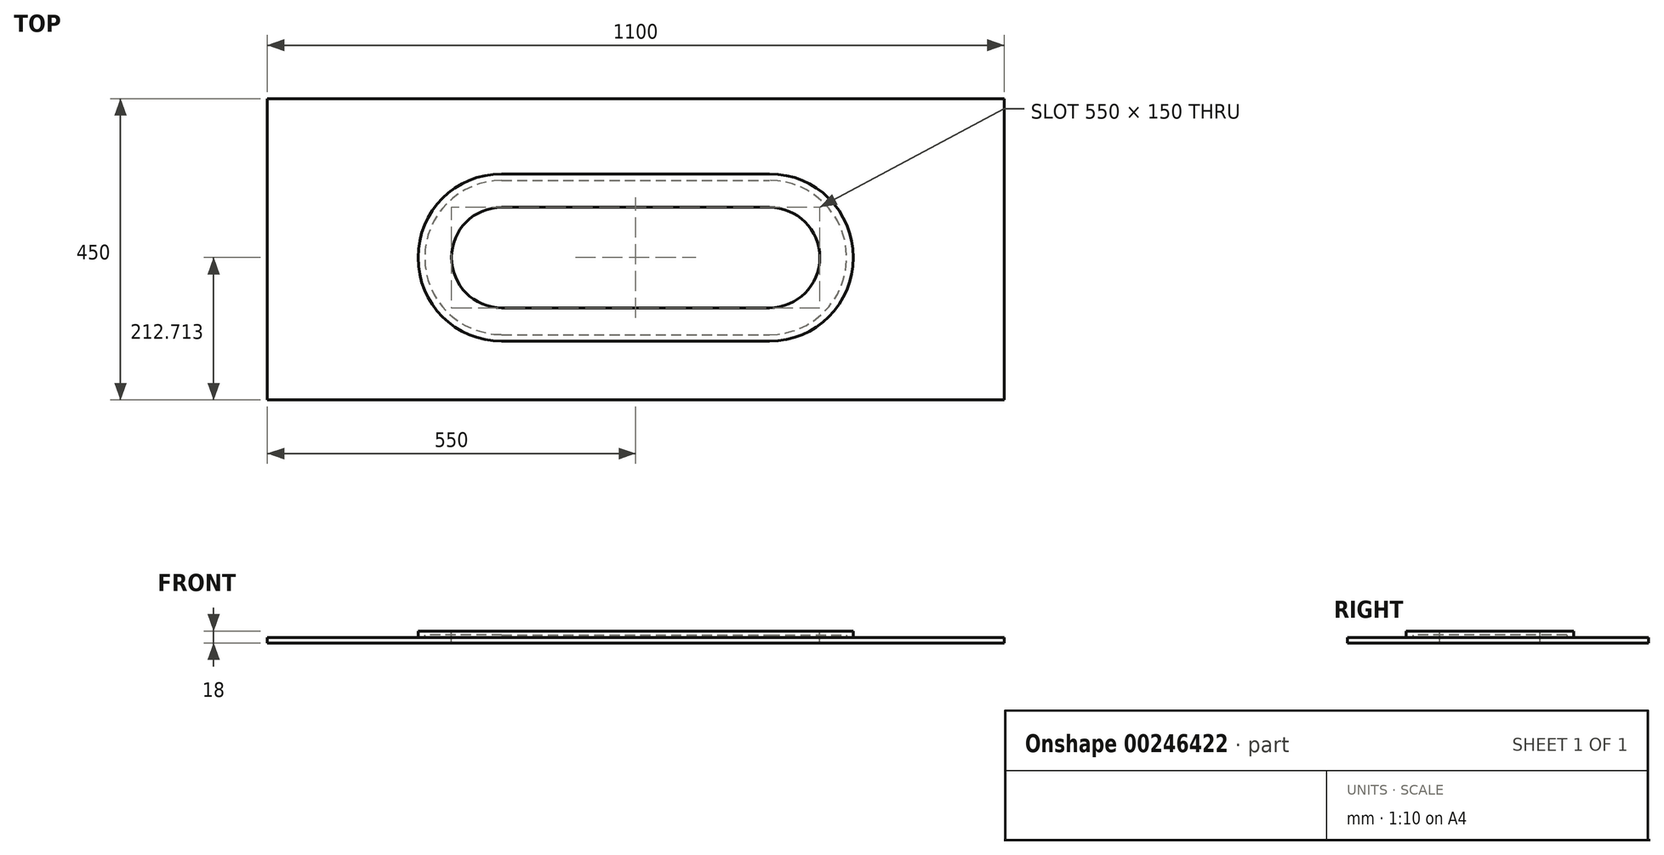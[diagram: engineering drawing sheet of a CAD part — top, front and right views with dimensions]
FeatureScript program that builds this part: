
annotation { "Feature Type Name" : "Feature", "Feature Type Description" : "" }
export const myFeature = defineFeature(function(context is Context, id is Id, definition is map)
    precondition{}
    {
        {
            var Q0;
            Q0=qCreatedBy(makeId("Top.planeOp"),FACE);
            var sketch = newSketch(context, id + "F0", { "sketchPlane" : qUnion([Q0])});
            skLineSegment(sketch, "E0.bottom", {"start": v(0, 0) * mm, "end": v(-1100, 0) * mm});
            skLineSegment(sketch, "E0.top", {"start": v(0, 450) * mm, "end": v(-1100, 450) * mm});
            skLineSegment(sketch, "E0.left", {"start": v(0, 0) * mm, "end": v(0, 450) * mm});
            skLineSegment(sketch, "E0.right", {"start": v(-1100, 0) * mm, "end": v(-1100, 450) * mm});
            skSolve(sketch);
        }
        {
            var Q0;
            Q0 = qSketchRegion(id + "F0", true);
            extrude(context, id + "F1", {"entities" : qUnion([Q0]), "depth" : 18 * mm});
        }
        {
            var Q0;
            Q0=makeQuery(id+"F1.opExtrude","CAP_FACE",FACE,{"disambiguationData":[OSD([sQuery(id+"F0.wireOp",EDGE,"E0.bottom"),sQuery(id+"F0.wireOp",EDGE,"E0.top"),sQuery(id+"F0.wireOp",EDGE,"E0.left"),sQuery(id+"F0.wireOp",EDGE,"E0.right")])],"isStart":false});
            var sketch = newSketch(context, id + "F2", { "sketchPlane" : qUnion([Q0])});
            skLineSegment(sketch, "E1.bottom", {"start": v(-750, 287.71) * mm, "end": v(-350, 287.71) * mm});
            skLineSegment(sketch, "E1.top", {"start": v(-750, 137.71) * mm, "end": v(-350, 137.71) * mm});
            skArc(sketch, "E2", {"start": v(-350, 287.71) * mm, "mid": v(-275, 212.71) * mm, "end": v(-350, 137.71) * mm});
            skArc(sketch, "E3", {"start": v(-750, 287.71) * mm, "mid": v(-825, 212.71) * mm, "end": v(-750, 137.71) * mm});
            skSolve(sketch);
        }
        {
            var Q0;
            Q0 = qSketchRegion(id + "F2", true);
            extrude(context, id + "F3", {"entities" : qUnion([Q0]), "operationType" : NewBodyOperationType.REMOVE, "endBound" : BoundingType.THROUGH_ALL, "oppositeDirection" : true, "depth" : 25 * mm});
        }
        {
            var Q0;
            Q0=makeQuery(id+"F1.opExtrude","CAP_FACE",FACE,{"disambiguationData":[OSD([sQuery(id+"F0.wireOp",EDGE,"E0.bottom"),sQuery(id+"F0.wireOp",EDGE,"E0.top"),sQuery(id+"F0.wireOp",EDGE,"E0.left"),sQuery(id+"F0.wireOp",EDGE,"E0.right")])],"isStart":false});
            var sketch = newSketch(context, id + "F4", { "sketchPlane" : qUnion([Q0])});
            skArc(sketch, "E4.0", {"start": v(-350, 337.71) * mm, "mid": v(-225, 212.71) * mm, "end": v(-350, 87.71) * mm});
            skLineSegment(sketch, "E4.1", {"start": v(-750, 337.71) * mm, "end": v(-350, 337.71) * mm});
            skArc(sketch, "E4.2", {"start": v(-750, 337.71) * mm, "mid": v(-875, 212.71) * mm, "end": v(-750, 87.71) * mm});
            skLineSegment(sketch, "E4.3", {"start": v(-750, 87.71) * mm, "end": v(-350, 87.71) * mm});
            skSolve(sketch);
        }
        {
            var Q0;
            Q0=makeQuery(id+"F4.imprint","IMPRINT",FACE,{"disambiguationData":[TD([[makeQuery(id+"F4.imprint","IMPRINT",EDGE,{"derivedFrom":sQuery(id+"F4.wireOp",EDGE,"E4.0")}),-1.0]])]});
            extrude(context, id + "F5", {"entities" : qUnion([Q0]), "operationType" : NewBodyOperationType.REMOVE, "oppositeDirection" : true, "depth" : 10 * mm});
        }
        {
            var Q0;
            Q0=makeQuery(id+"F5.boolean.opBoolean","COPY",FACE,{"derivedFrom":makeQuery(id+"F5.opExtrude","CAP_FACE",FACE,{"disambiguationData":[OSD([sQuery(id+"F2.wireOp",EDGE,"E1.bottom"),sQuery(id+"F2.wireOp",EDGE,"E1.top"),sQuery(id+"F2.wireOp",EDGE,"E2"),sQuery(id+"F2.wireOp",EDGE,"E3"),sQuery(id+"F4.wireOp",EDGE,"E4.0"),sQuery(id+"F4.wireOp",EDGE,"E4.1"),sQuery(id+"F4.wireOp",EDGE,"E4.2"),sQuery(id+"F4.wireOp",EDGE,"E4.3")])],"isStart":false})});
            var sketch = newSketch(context, id + "F6", { "sketchPlane" : qUnion([Q0])});
            skArc(sketch, "E5.0", {"start": v(-750, 327.71) * mm, "mid": v(-865, 212.71) * mm, "end": v(-750, 97.71) * mm});
            skLineSegment(sketch, "E5.1", {"start": v(-750, 327.71) * mm, "end": v(-350, 327.71) * mm});
            skArc(sketch, "E5.2", {"start": v(-350, 327.71) * mm, "mid": v(-235, 212.71) * mm, "end": v(-350, 97.71) * mm});
            skLineSegment(sketch, "E5.3", {"start": v(-750, 97.71) * mm, "end": v(-350, 97.71) * mm});
            skSolve(sketch);
        }
        {
            var Q0;
            Q0 = qSketchRegion(id + "F6", true);
            extrude(context, id + "F7", {"entities" : qUnion([Q0]), "depth" : 4 * mm});
        }
    });
